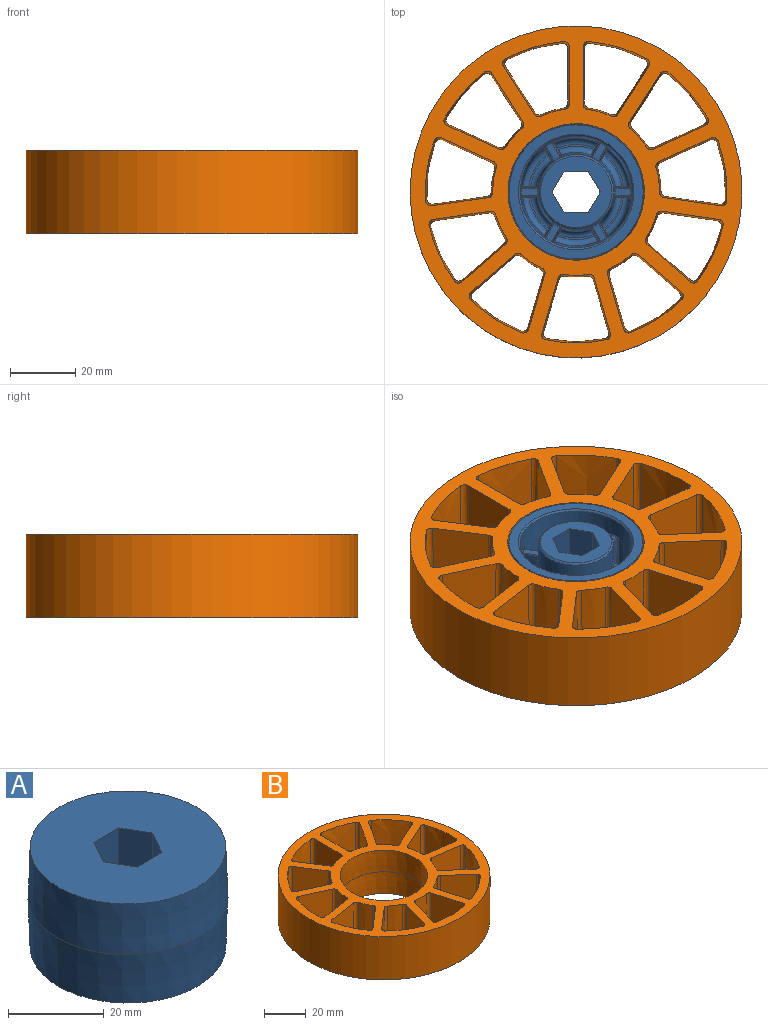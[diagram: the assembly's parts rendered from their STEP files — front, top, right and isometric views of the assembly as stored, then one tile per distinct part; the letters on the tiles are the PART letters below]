
ASSEMBLY  parts=2 mates=1
PART A: 159 faces, bbox 41.9x41.9x25.4 mm
  f0: torus R=16.68mm, axis (0,0,1), area 0.8mm2, adj f6,f31,f40,f45
  f1: torus R=11.9mm, axis (0,0,1), area 0.8mm2, adj f7,f31,f36,f41
  f2: cone r=20.24mm half-angle=2deg, axis (0,0,-1), area 1655.4mm2, adj f3,f25
  f3: cone r=20.96mm half-angle=2deg, axis (0,0,1), area 1655.4mm2, adj f2,f26
  f4: cone r=10.9mm half-angle=47deg, axis (0,0,1), area 52.3mm2, adj f7,f24
  f5: cone r=17.13mm half-angle=45deg, axis (0,0,-1), area 81.3mm2, adj f6,f26
  f6: cone r=16.46mm half-angle=2deg, axis (0,0,-1), area 1757.7mm2, adj f0,f5,f9,f12,f15,f18,f21,f27
  f7: cone r=11.43mm half-angle=2deg, axis (0,0,1), area 1163.6mm2, adj f1,f4,f8,f11,f14,f17,f20,f23
  f8: torus R=14.02mm, axis (0,0,-1), area 29mm2, adj f7,f10,f32,f146
  f9: torus R=14.55mm, axis (0,0,-1), area 37.6mm2, adj f6,f10,f35,f151
  f10: plane 9.83x5.94mm, normal (0,0,-1), area 6mm2, adj f8,f9,f33,f149
  f11: torus R=14.02mm, axis (0,0,-1), area 29mm2, adj f7,f13,f128,f135
  f12: torus R=14.55mm, axis (0,0,-1), area 37.6mm2, adj f6,f13,f133,f138
  f13: plane 11.35x1.61mm, normal (0,0,-1), area 6mm2, adj f11,f12,f131,f136
  f14: torus R=14.02mm, axis (0,0,-1), area 29mm2, adj f7,f16,f110,f117
  f15: torus R=14.55mm, axis (0,0,-1), area 37.6mm2, adj f6,f16,f115,f120
  f16: plane 9.83x5.94mm, normal (0,0,-1), area 6mm2, adj f14,f15,f113,f118
  f17: torus R=14.02mm, axis (0,0,-1), area 29mm2, adj f7,f19,f92,f99
  f18: torus R=14.55mm, axis (0,0,-1), area 37.6mm2, adj f6,f19,f97,f102
  f19: plane 9.83x5.94mm, normal (0,0,-1), area 6mm2, adj f17,f18,f95,f100
  f20: torus R=14.02mm, axis (0,0,-1), area 29mm2, adj f7,f22,f74,f81
  f21: torus R=14.55mm, axis (0,0,-1), area 37.6mm2, adj f6,f22,f79,f84
  f22: plane 11.35x1.61mm, normal (0,0,-1), area 6mm2, adj f20,f21,f77,f82
  f23: torus R=14.02mm, axis (0,0,-1), area 29mm2, adj f7,f28,f42,f63
  f24: plane 21.81x21.81mm, normal (0,0,-1), area 232.7mm2, adj f4,f153,f154,f155,f156,f157,f158
  f25: plane 41.02x41.02mm, normal (0,0,1), area 1180.9mm2, adj f2,f153,f154,f155,f156,f157,f158
  f26: plane 41.02x41.02mm, normal (0,0,-1), area 342.7mm2, adj f3,f5
  f27: torus R=14.55mm, axis (0,0,-1), area 37.6mm2, adj f6,f28,f46,f66
  f28: plane 9.83x5.94mm, normal (0,0,-1), area 6mm2, adj f23,f27,f44,f64
  f29: plane 14.75x4.78mm, normal (0,-1,-0.02), area 61.7mm2, adj f39,f42,f43,f44,f46,f47
  f30: plane 14.74x4.78mm, normal (0,1,-0.02), area 61.7mm2, adj f32,f33,f34,f35,f37,f38
  f31: plane 4.82x2.04mm, normal (0,0,-1), area 9.8mm2, adj f0,f1,f38,f43
  f32: bspline ~1.91x1.84mm, area 1mm2, adj f8,f30,f33,f34
  f33: cylinder r=0.25mm len=0.53mm, axis (-1,0,0), area 0.2mm2, adj f10,f30,f32,f35
  f34: bspline ~13.15x0.68mm, area 4.8mm2, adj f7,f30,f32,f36
  f35: bspline ~1.95x1.85mm, area 1.2mm2, adj f9,f30,f33,f37
  f36: bspline ~0.5x0.5mm, area 0.2mm2, adj f1,f7,f34,f38
  f37: bspline ~13.15x0.74mm, area 5.6mm2, adj f6,f30,f35,f40
  f38: cylinder r=0.25mm len=4.83mm, axis (-1,0,0), area 1.9mm2, adj f30,f31,f36,f40
  f39: cylinder r=0.25mm len=13.15mm, axis (0.03,-0.02,1), area 4.8mm2, adj f7,f29,f41,f42
  f40: bspline ~0.53x0.51mm, area 0.2mm2, adj f0,f6,f37,f38
  f41: bspline ~0.5x0.5mm, area 0.2mm2, adj f1,f7,f39,f43
  f42: bspline ~1.91x1.84mm, area 1mm2, adj f23,f29,f39,f44
  f43: cylinder r=0.25mm len=4.83mm, axis (1,0,0), area 1.9mm2, adj f29,f31,f41,f45
  f44: cylinder r=0.25mm len=0.53mm, axis (1,0,0), area 0.2mm2, adj f28,f29,f42,f46
  f45: bspline ~0.53x0.51mm, area 0.2mm2, adj f0,f6,f43,f47
  f46: bspline ~1.95x1.85mm, area 1.2mm2, adj f27,f29,f44,f47
  f47: bspline ~13.15x0.74mm, area 5.6mm2, adj f6,f29,f45,f46
  f48: plane 14.75x4.14mm, normal (-0.87,-0.5,-0.02), area 61.7mm2, adj f71,f74,f76,f77,f79,f80
  f49: plane 14.74x4.14mm, normal (0.87,0.5,-0.02), area 61.7mm2, adj f63,f64,f65,f66,f68,f69
  f50: plane 5.17x4.16mm, normal (0,0,-1), area 9.8mm2, adj f69,f70,f75,f76
  f51: plane 14.75x4.14mm, normal (-0.87,0.5,-0.02), area 61.7mm2, adj f89,f92,f94,f95,f97,f98
  f52: plane 14.74x4.14mm, normal (0.87,-0.5,-0.02), area 61.7mm2, adj f81,f82,f83,f84,f86,f87
  f53: plane 5.17x4.16mm, normal (0,0,-1), area 9.8mm2, adj f87,f88,f93,f94
  f54: plane 14.75x4.78mm, normal (0,1,-0.02), area 61.7mm2, adj f107,f110,f112,f113,f115,f116
  f55: plane 14.74x4.78mm, normal (0,-1,-0.02), area 61.7mm2, adj f99,f100,f101,f102,f104,f105
  f56: plane 4.82x2.04mm, normal (0,0,-1), area 9.8mm2, adj f105,f106,f111,f112
  f57: plane 14.75x4.14mm, normal (0.87,0.5,-0.02), area 61.7mm2, adj f125,f128,f130,f131,f133,f134
  f58: plane 14.74x4.14mm, normal (-0.87,-0.5,-0.02), area 61.7mm2, adj f117,f118,f119,f120,f122,f123
  f59: plane 5.17x4.16mm, normal (0,0,-1), area 9.8mm2, adj f123,f124,f129,f130
  f60: plane 14.75x4.14mm, normal (0.87,-0.5,-0.02), area 61.7mm2, adj f143,f146,f148,f149,f151,f152
  f61: plane 14.74x4.14mm, normal (-0.87,0.5,-0.02), area 61.7mm2, adj f135,f136,f137,f138,f140,f141
  f62: plane 5.17x4.16mm, normal (0,0,-1), area 9.8mm2, adj f141,f142,f147,f148
  f63: bspline ~1.84x1.75mm, area 1mm2, adj f23,f49,f64,f65
  f64: cylinder r=0.25mm len=0.59mm, axis (-0.5,0.87,0), area 0.2mm2, adj f28,f49,f63,f66
  f65: bspline ~13.15x0.59mm, area 4.8mm2, adj f7,f49,f63,f67
  f66: bspline ~1.85x1.83mm, area 1.2mm2, adj f27,f49,f64,f68
  f67: bspline ~0.5x0.49mm, area 0.2mm2, adj f7,f65,f69,f70
  f68: bspline ~13.15x0.66mm, area 5.6mm2, adj f6,f49,f66,f72
  f69: cylinder r=0.25mm len=4.31mm, axis (-0.5,0.87,0), area 1.9mm2, adj f49,f50,f67,f72
  f70: torus R=11.9mm, axis (0,0,1), area 0.8mm2, adj f7,f50,f67,f73
  f71: cylinder r=0.25mm len=13.15mm, axis (0,-0.04,1), area 4.8mm2, adj f7,f48,f73,f74
  f72: bspline ~0.56x0.51mm, area 0.2mm2, adj f6,f68,f69,f75
  f73: bspline ~0.56x0.5mm, area 0.2mm2, adj f7,f70,f71,f76
  f74: bspline ~1.84x1.77mm, area 1mm2, adj f20,f48,f71,f77
  f75: torus R=16.68mm, axis (0,0,1), area 0.8mm2, adj f6,f50,f72,f78
  f76: cylinder r=0.25mm len=4.31mm, axis (0.5,-0.87,0), area 1.9mm2, adj f48,f50,f73,f78
  f77: cylinder r=0.25mm len=0.59mm, axis (0.5,-0.87,0), area 0.2mm2, adj f22,f48,f74,f79
  f78: bspline ~0.51x0.48mm, area 0.2mm2, adj f6,f75,f76,f80
  f79: bspline ~1.85x1.79mm, area 1.2mm2, adj f21,f48,f77,f80
  f80: bspline ~13.16x0.7mm, area 5.6mm2, adj f6,f48,f78,f79
  f81: bspline ~1.84x1.77mm, area 1mm2, adj f20,f52,f82,f83
  f82: cylinder r=0.25mm len=0.59mm, axis (-0.5,-0.87,0), area 0.2mm2, adj f22,f52,f81,f84
  f83: bspline ~13.15x0.61mm, area 4.8mm2, adj f7,f52,f81,f85
  f84: bspline ~1.85x1.79mm, area 1.2mm2, adj f21,f52,f82,f86
  f85: bspline ~0.56x0.5mm, area 0.2mm2, adj f7,f83,f87,f88
  f86: bspline ~13.15x0.66mm, area 5.6mm2, adj f6,f52,f84,f90
  f87: cylinder r=0.25mm len=4.31mm, axis (0.5,0.87,0), area 1.9mm2, adj f52,f53,f85,f90
  f88: torus R=11.9mm, axis (0,0,1), area 0.8mm2, adj f7,f53,f85,f91
  f89: cylinder r=0.25mm len=13.15mm, axis (-0.03,-0.02,1), area 4.8mm2, adj f7,f51,f91,f92
  f90: bspline ~0.51x0.48mm, area 0.2mm2, adj f6,f86,f87,f93
  f91: bspline ~0.5x0.49mm, area 0.2mm2, adj f7,f88,f89,f94
  f92: bspline ~1.84x1.75mm, area 1mm2, adj f17,f51,f89,f95
  f93: torus R=16.68mm, axis (0,0,1), area 0.8mm2, adj f6,f53,f90,f96
  f94: cylinder r=0.25mm len=4.31mm, axis (-0.5,-0.87,0), area 1.9mm2, adj f51,f53,f91,f96
  f95: cylinder r=0.25mm len=0.59mm, axis (0.5,0.87,0), area 0.2mm2, adj f19,f51,f92,f97
  f96: bspline ~0.56x0.51mm, area 0.2mm2, adj f6,f93,f94,f98
  f97: bspline ~1.85x1.83mm, area 1.2mm2, adj f18,f51,f95,f98
  f98: bspline ~13.15x0.66mm, area 5.6mm2, adj f6,f51,f96,f97
  f99: bspline ~1.91x1.84mm, area 1mm2, adj f17,f55,f100,f101
  f100: cylinder r=0.25mm len=0.53mm, axis (-1,0,0), area 0.2mm2, adj f19,f55,f99,f102
  f101: bspline ~13.15x0.68mm, area 4.8mm2, adj f7,f55,f99,f103
  f102: bspline ~1.95x1.85mm, area 1.2mm2, adj f18,f55,f100,f104
  f103: bspline ~0.5x0.5mm, area 0.2mm2, adj f7,f101,f105,f106
  f104: bspline ~13.15x0.74mm, area 5.6mm2, adj f6,f55,f102,f108
  f105: cylinder r=0.25mm len=4.83mm, axis (1,0,0), area 1.9mm2, adj f55,f56,f103,f108
  f106: torus R=11.9mm, axis (0,0,1), area 0.8mm2, adj f7,f56,f103,f109
  f107: cylinder r=0.25mm len=13.15mm, axis (-0.03,0.02,1), area 4.8mm2, adj f7,f54,f109,f110
  f108: bspline ~0.53x0.51mm, area 0.2mm2, adj f6,f104,f105,f111
  f109: bspline ~0.5x0.5mm, area 0.2mm2, adj f7,f106,f107,f112
  f110: bspline ~1.91x1.84mm, area 1mm2, adj f14,f54,f107,f113
  f111: torus R=16.68mm, axis (0,0,1), area 0.8mm2, adj f6,f56,f108,f114
  f112: cylinder r=0.25mm len=4.83mm, axis (-1,0,0), area 1.9mm2, adj f54,f56,f109,f114
  f113: cylinder r=0.25mm len=0.53mm, axis (1,0,0), area 0.2mm2, adj f16,f54,f110,f115
  f114: bspline ~0.53x0.51mm, area 0.2mm2, adj f6,f111,f112,f116
  f115: bspline ~1.95x1.85mm, area 1.2mm2, adj f15,f54,f113,f116
  f116: bspline ~13.15x0.74mm, area 5.6mm2, adj f6,f54,f114,f115
  f117: bspline ~1.84x1.75mm, area 1mm2, adj f14,f58,f118,f119
  f118: cylinder r=0.25mm len=0.59mm, axis (-0.5,0.87,0), area 0.2mm2, adj f16,f58,f117,f120
  f119: bspline ~13.15x0.59mm, area 4.8mm2, adj f7,f58,f117,f121
  f120: bspline ~1.85x1.83mm, area 1.2mm2, adj f15,f58,f118,f122
  f121: bspline ~0.5x0.49mm, area 0.2mm2, adj f7,f119,f123,f124
  f122: bspline ~13.15x0.66mm, area 5.6mm2, adj f6,f58,f120,f126
  f123: cylinder r=0.25mm len=4.31mm, axis (0.5,-0.87,0), area 1.9mm2, adj f58,f59,f121,f126
  f124: torus R=11.9mm, axis (0,0,1), area 0.8mm2, adj f7,f59,f121,f127
  f125: cylinder r=0.25mm len=13.15mm, axis (0,0.04,1), area 4.8mm2, adj f7,f57,f127,f128
  f126: bspline ~0.56x0.51mm, area 0.2mm2, adj f6,f122,f123,f129
  f127: bspline ~0.56x0.5mm, area 0.2mm2, adj f7,f124,f125,f130
  f128: bspline ~1.84x1.77mm, area 1mm2, adj f11,f57,f125,f131
  f129: torus R=16.68mm, axis (0,0,1), area 0.8mm2, adj f6,f59,f126,f132
  f130: cylinder r=0.25mm len=4.31mm, axis (-0.5,0.87,0), area 1.9mm2, adj f57,f59,f127,f132
  f131: cylinder r=0.25mm len=0.59mm, axis (0.5,-0.87,0), area 0.2mm2, adj f13,f57,f128,f133
  f132: bspline ~0.51x0.48mm, area 0.2mm2, adj f6,f129,f130,f134
  f133: bspline ~1.85x1.79mm, area 1.2mm2, adj f12,f57,f131,f134
  f134: bspline ~13.16x0.7mm, area 5.6mm2, adj f6,f57,f132,f133
  f135: bspline ~1.84x1.77mm, area 1mm2, adj f11,f61,f136,f137
  f136: cylinder r=0.25mm len=0.59mm, axis (0.5,0.87,0), area 0.2mm2, adj f13,f61,f135,f138
  f137: bspline ~13.15x0.68mm, area 4.8mm2, adj f7,f61,f135,f139
  f138: bspline ~1.85x1.79mm, area 1.2mm2, adj f12,f61,f136,f140
  f139: bspline ~0.56x0.5mm, area 0.2mm2, adj f7,f137,f141,f142
  f140: bspline ~13.15x0.66mm, area 5.6mm2, adj f6,f61,f138,f144
  f141: cylinder r=0.25mm len=4.31mm, axis (-0.5,-0.87,0), area 1.9mm2, adj f61,f62,f139,f144
  f142: torus R=11.9mm, axis (0,0,1), area 0.8mm2, adj f7,f62,f139,f145
  f143: cylinder r=0.25mm len=13.15mm, axis (0.03,0.02,1), area 4.8mm2, adj f7,f60,f145,f146
  f144: bspline ~0.51x0.48mm, area 0.2mm2, adj f6,f140,f141,f147
  f145: bspline ~0.5x0.49mm, area 0.2mm2, adj f7,f142,f143,f148
  f146: bspline ~1.84x1.75mm, area 1mm2, adj f8,f60,f143,f149
  f147: torus R=16.68mm, axis (0,0,1), area 0.8mm2, adj f6,f62,f144,f150
  f148: cylinder r=0.25mm len=4.31mm, axis (0.5,0.87,0), area 1.9mm2, adj f60,f62,f145,f150
  f149: cylinder r=0.25mm len=0.59mm, axis (-0.5,-0.87,0), area 0.2mm2, adj f10,f60,f146,f151
  f150: bspline ~0.56x0.51mm, area 0.2mm2, adj f6,f147,f148,f152
  f151: bspline ~1.85x1.83mm, area 1.2mm2, adj f9,f60,f149,f152
  f152: bspline ~13.15x0.66mm, area 5.6mm2, adj f6,f60,f150,f151
  f153: plane 25.4x6.38mm, normal (0.87,0.5,0), area 187mm2, adj f24,f25,f154,f158
  f154: plane 25.4x7.36mm, normal (0,1,0), area 187mm2, adj f24,f25,f153,f155
  f155: plane 25.4x6.38mm, normal (-0.87,0.5,0), area 187mm2, adj f24,f25,f154,f156
  f156: plane 25.4x6.38mm, normal (-0.87,-0.5,0), area 187mm2, adj f24,f25,f155,f157
  f157: plane 25.4x7.36mm, normal (0,-1,0), area 187mm2, adj f24,f25,f156,f158
  f158: plane 25.4x6.38mm, normal (0.87,-0.5,0), area 187mm2, adj f24,f25,f153,f157
PART B: 93 faces, bbox 101.7x101.7x25.8 mm
  f0: cylinder r=50.8mm len=101.6mm, axis (0,0,-1), area 8107.3mm2, adj f25,f27
  f1: cone r=20.96mm half-angle=0.3deg, axis (0,0,1), area 1669.7mm2, adj f2,f27
  f2: cone r=20.89mm half-angle=0.3deg, axis (0,0,-1), area 1669.7mm2, adj f1,f25
  f3: cone r=45.72mm half-angle=1deg, axis (0,0,1), area 460.8mm2, adj f25,f27,f58,f59
  f4: cone r=25.97mm half-angle=1deg, axis (0,0,-1), area 186.1mm2, adj f25,f27,f80,f81
  f5: cone r=25.97mm half-angle=1deg, axis (0,0,-1), area 186.2mm2, adj f25,f27,f88,f89
  f6: cone r=45.72mm half-angle=1deg, axis (0,0,1), area 460.8mm2, adj f25,f27,f90,f91
  f7: cone r=45.72mm half-angle=1deg, axis (0,0,1), area 460.8mm2, adj f25,f27,f82,f83
  f8: cone r=25.97mm half-angle=1deg, axis (0,0,-1), area 186.2mm2, adj f25,f27,f76,f77
  f9: cone r=45.72mm half-angle=1deg, axis (0,0,1), area 460.8mm2, adj f25,f27,f78,f79
  f10: cone r=25.97mm half-angle=1deg, axis (0,0,-1), area 186.2mm2, adj f25,f27,f72,f73
  f11: cone r=45.72mm half-angle=1deg, axis (0,0,1), area 460.8mm2, adj f25,f27,f74,f75
  f12: cone r=25.97mm half-angle=1deg, axis (0,0,-1), area 186.2mm2, adj f25,f27,f68,f69
  f13: cone r=45.72mm half-angle=1deg, axis (0,0,1), area 460.8mm2, adj f25,f27,f70,f71
  f14: cone r=25.97mm half-angle=1deg, axis (0,0,-1), area 186.2mm2, adj f25,f27,f64,f65
  f15: cone r=45.72mm half-angle=1deg, axis (0,0,1), area 460.8mm2, adj f25,f27,f66,f67
  f16: cone r=25.97mm half-angle=1deg, axis (0,0,-1), area 186.2mm2, adj f25,f27,f60,f61
  f17: cone r=45.72mm half-angle=1deg, axis (0,0,1), area 460.8mm2, adj f25,f27,f62,f63
  f18: cone r=25.97mm half-angle=1deg, axis (0,0,-1), area 186.2mm2, adj f25,f27,f56,f57
  f19: cone r=25.97mm half-angle=1deg, axis (0,0,-1), area 186.2mm2, adj f25,f27,f52,f53
  f20: cone r=45.72mm half-angle=1deg, axis (0,0,1), area 460.8mm2, adj f25,f27,f54,f55
  f21: cone r=25.97mm half-angle=1deg, axis (0,0,-1), area 186.2mm2, adj f25,f27,f49,f50
  f22: cone r=45.72mm half-angle=1deg, axis (0,0,1), area 460.8mm2, adj f25,f27,f51,f92
  f23: plane 25.4x17.56mm, normal (1,0,0.02), area 435mm2, adj f25,f27,f85,f86
  f24: plane 25.4x17.56mm, normal (-1,0,0.02), area 435mm2, adj f25,f27,f50,f92
  f25: plane 101.66x101.66mm, normal (0,0,1), area 3063.9mm2, adj f0,f2,f3,f4,f5,f6,f7,f8
  f26: cone r=25.97mm half-angle=1deg, axis (0,0,-1), area 186.2mm2, adj f25,f27,f86,f87
  f27: plane 101.66x101.66mm, normal (0,0,-1), area 3415.8mm2, adj f0,f1,f3,f4,f5,f6,f7,f8
  f28: cone r=45.72mm half-angle=1deg, axis (0,0,1), area 460.8mm2, adj f25,f27,f84,f85
  f29: plane 25.4x14.77mm, normal (0.84,0.54,0.02), area 435mm2, adj f25,f27,f49,f51
  f30: plane 25.4x14.77mm, normal (-0.84,-0.54,0.02), area 435mm2, adj f25,f27,f53,f54
  f31: plane 25.4x15.97mm, normal (0.42,0.91,0.02), area 435mm2, adj f25,f27,f52,f55
  f32: plane 25.4x15.97mm, normal (-0.42,-0.91,0.02), area 435mm2, adj f25,f27,f57,f58
  f33: plane 25.4x17.38mm, normal (-0.14,0.99,0.02), area 435mm2, adj f25,f27,f56,f59
  f34: plane 25.4x17.38mm, normal (0.14,-0.99,0.02), area 435mm2, adj f25,f27,f61,f62
  f35: plane 25.4x13.27mm, normal (-0.65,0.76,0.02), area 435mm2, adj f25,f27,f60,f63
  f36: plane 25.4x13.27mm, normal (0.65,-0.76,0.02), area 435mm2, adj f25,f27,f65,f66
  f37: plane 25.4x16.85mm, normal (-0.96,0.28,0.02), area 435mm2, adj f25,f27,f64,f67
  f38: plane 25.4x16.85mm, normal (0.96,-0.28,0.02), area 435mm2, adj f25,f27,f69,f70
  f39: plane 25.4x16.85mm, normal (-0.96,-0.28,0.02), area 435mm2, adj f25,f27,f68,f71
  f40: plane 25.4x16.85mm, normal (0.96,0.28,0.02), area 435mm2, adj f25,f27,f73,f74
  f41: plane 25.4x13.27mm, normal (-0.65,-0.76,0.02), area 435mm2, adj f25,f27,f72,f75
  f42: plane 25.4x13.27mm, normal (0.65,0.76,0.02), area 435mm2, adj f25,f27,f77,f78
  f43: plane 25.4x17.38mm, normal (-0.14,-0.99,0.02), area 435mm2, adj f25,f27,f76,f79
  f44: plane 25.4x17.38mm, normal (0.14,0.99,0.02), area 435mm2, adj f25,f27,f81,f82
  f45: plane 25.4x15.97mm, normal (0.42,-0.91,0.02), area 435mm2, adj f25,f27,f80,f83
  f46: plane 25.4x15.97mm, normal (-0.42,0.91,0.02), area 435mm2, adj f25,f27,f89,f90
  f47: plane 25.4x14.77mm, normal (0.84,-0.54,0.02), area 435mm2, adj f25,f27,f88,f91
  f48: plane 25.4x14.77mm, normal (-0.84,0.54,0.02), area 435mm2, adj f25,f27,f84,f87
  f49: bspline ~25.41x2.15mm, area 57.6mm2, adj f21,f25,f27,f29
  f50: bspline ~25.41x1.96mm, area 57.6mm2, adj f21,f24,f25,f27
  f51: bspline ~25.41x2.43mm, area 66.9mm2, adj f22,f25,f27,f29
  f52: bspline ~25.41x2.17mm, area 57.6mm2, adj f19,f25,f27,f31
  f53: bspline ~25.41x2.15mm, area 57.6mm2, adj f19,f25,f27,f30
  f54: bspline ~25.75x2.43mm, area 66.9mm2, adj f20,f25,f27,f30
  f55: bspline ~25.75x2.44mm, area 66.9mm2, adj f20,f25,f27,f31
  f56: bspline ~25.73x1.95mm, area 57.6mm2, adj f18,f25,f27,f33
  f57: bspline ~25.73x2.13mm, area 57.6mm2, adj f18,f25,f27,f32
  f58: bspline ~25.75x2.41mm, area 66.9mm2, adj f3,f25,f27,f32
  f59: bspline ~25.41x2.23mm, area 66.9mm2, adj f3,f25,f27,f33
  f60: bspline ~25.73x2.13mm, area 57.6mm2, adj f16,f25,f27,f35
  f61: bspline ~25.41x2.07mm, area 57.6mm2, adj f16,f25,f27,f34
  f62: bspline ~25.41x2.31mm, area 66.9mm2, adj f17,f25,f27,f34
  f63: bspline ~25.75x2.4mm, area 66.9mm2, adj f17,f25,f27,f35
  f64: bspline ~25.73x2.14mm, area 57.6mm2, adj f14,f25,f27,f37
  f65: bspline ~25.73x2.09mm, area 57.6mm2, adj f14,f25,f27,f36
  f66: bspline ~25.41x2.36mm, area 66.9mm2, adj f15,f25,f27,f36
  f67: bspline ~25.75x2.4mm, area 66.9mm2, adj f15,f25,f27,f37
  f68: bspline ~25.41x2.05mm, area 57.6mm2, adj f12,f25,f27,f39
  f69: bspline ~25.41x2.05mm, area 57.6mm2, adj f12,f25,f27,f38
  f70: bspline ~25.41x2.34mm, area 66.9mm2, adj f13,f25,f27,f38
  f71: bspline ~25.41x2.34mm, area 66.9mm2, adj f13,f25,f27,f39
  f72: bspline ~25.73x2.09mm, area 57.6mm2, adj f10,f25,f27,f41
  f73: bspline ~25.73x2.14mm, area 57.6mm2, adj f10,f25,f27,f40
  f74: bspline ~25.75x2.4mm, area 66.9mm2, adj f11,f25,f27,f40
  f75: bspline ~25.41x2.36mm, area 66.9mm2, adj f11,f25,f27,f41
  f76: bspline ~25.41x2.07mm, area 57.6mm2, adj f8,f25,f27,f43
  f77: bspline ~25.73x2.13mm, area 57.6mm2, adj f8,f25,f27,f42
  f78: bspline ~25.75x2.4mm, area 66.9mm2, adj f9,f25,f27,f42
  f79: bspline ~25.41x2.31mm, area 66.9mm2, adj f9,f25,f27,f43
  f80: bspline ~25.73x2.13mm, area 57.6mm2, adj f4,f25,f27,f45
  f81: bspline ~25.41x1.94mm, area 57.6mm2, adj f4,f25,f27,f44
  f82: bspline ~25.41x2.23mm, area 66.9mm2, adj f7,f25,f27,f44
  f83: bspline ~25.75x2.41mm, area 66.9mm2, adj f7,f25,f27,f45
  f84: bspline ~25.41x2.43mm, area 66.9mm2, adj f25,f27,f28,f48
  f85: bspline ~25.41x2.18mm, area 66.9mm2, adj f23,f25,f27,f28
  f86: bspline ~25.41x1.96mm, area 57.6mm2, adj f23,f25,f26,f27
  f87: bspline ~25.41x2.15mm, area 57.6mm2, adj f25,f26,f27,f48
  f88: bspline ~25.41x2.15mm, area 57.6mm2, adj f5,f25,f27,f47
  f89: bspline ~25.41x2.17mm, area 57.6mm2, adj f5,f25,f27,f46
  f90: bspline ~25.75x2.44mm, area 66.9mm2, adj f6,f25,f27,f46
  f91: bspline ~25.75x2.43mm, area 66.9mm2, adj f6,f25,f27,f47
  f92: bspline ~25.41x2.18mm, area 66.9mm2, adj f22,f24,f25,f27
PLACE A rot(axis=(0,-1,0),180deg) t=(-16.24,3.85,-0.4)mm
PLACE B t=(-16.24,3.85,12.3)mm
MATE fastened A.f5 <-> B.f0  axis (0,0,-1) through (-16.24,3.85,-13.1)mm
